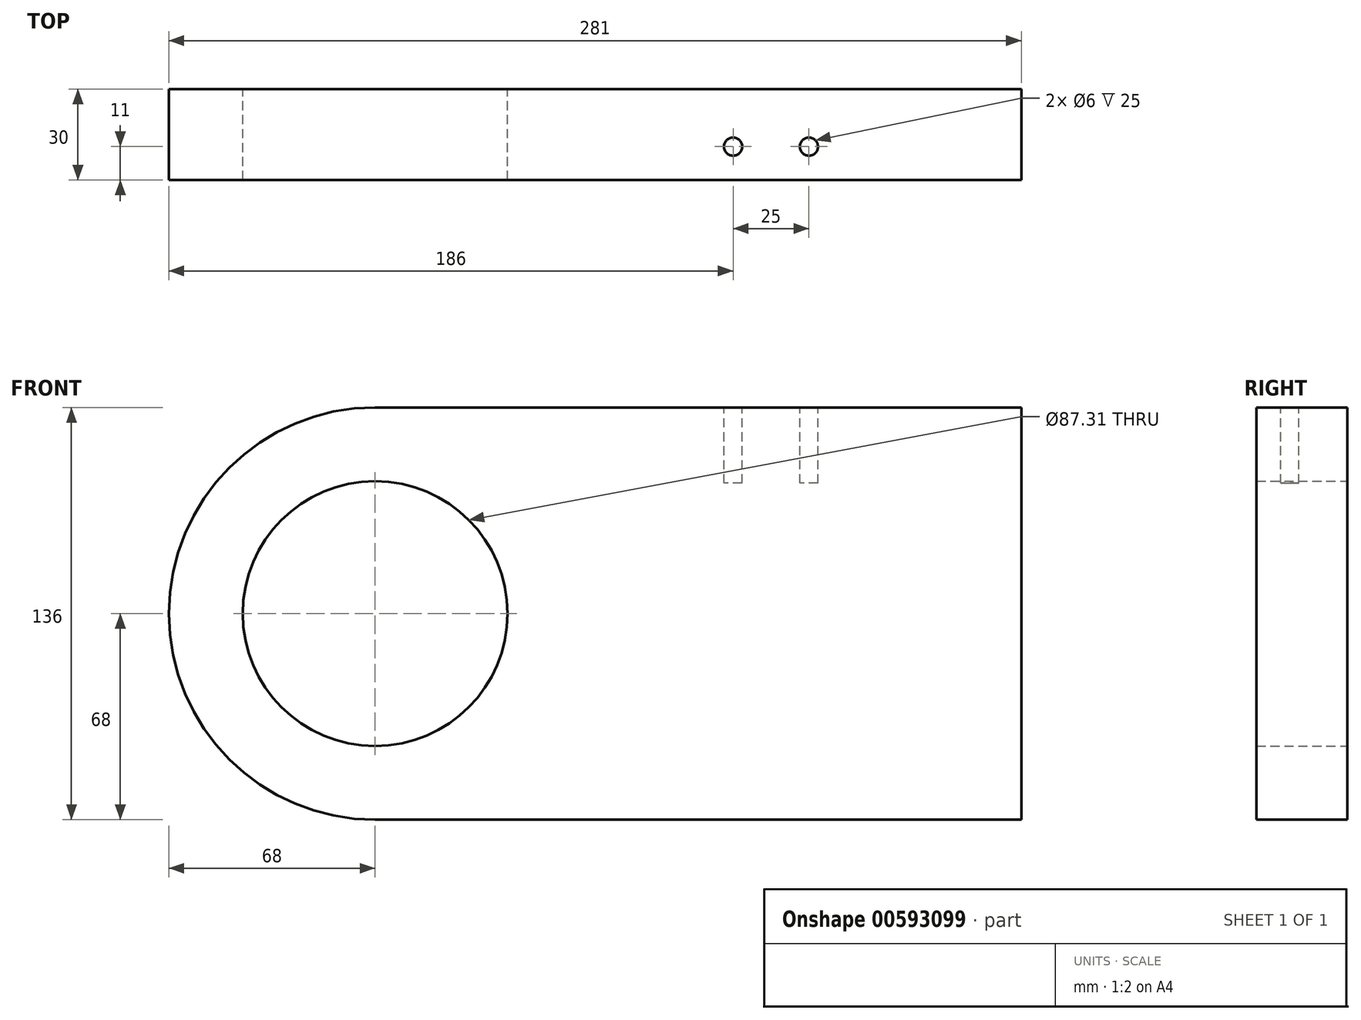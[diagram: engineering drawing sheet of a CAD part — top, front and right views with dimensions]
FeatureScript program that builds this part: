
annotation { "Feature Type Name" : "Feature", "Feature Type Description" : "" }
export const myFeature = defineFeature(function(context is Context, id is Id, definition is map)
    precondition{}
    {
        {
            var Q0;
            Q0=qCreatedBy(makeId("Front.planeOp"),FACE);
            var sketch = newSketch(context, id + "F0", { "sketchPlane" : qUnion([Q0])});
            skLineSegment(sketch, "E0.bottom", {"start": v(106.5, 68) * mm, "end": v(-106.5, 68) * mm});
            skLineSegment(sketch, "E0.top", {"start": v(106.5, -68) * mm, "end": v(-106.5, -68) * mm});
            skLineSegment(sketch, "E0.left", {"start": v(106.5, 68) * mm, "end": v(106.5, -68) * mm});
            skArc(sketch, "E1", {"start": v(-106.5, 68) * mm, "mid": v(-174.5, 0) * mm, "end": v(-106.5, -68) * mm});
            skCircle(sketch, "E2", {"center": v(-106.5, 0) * mm, "radius": 43.66 * mm});
            skSolve(sketch);
        }
        {
            var Q0;
            Q0=makeQuery(id+"F0.imprint","IMPRINT",FACE,{"disambiguationData":[TD([[makeQuery(id+"F0.imprint","IMPRINT",EDGE,{"derivedFrom":sQuery(id+"F0.wireOp",EDGE,"E0.bottom")}),1.0]])]});
            extrude(context, id + "F1", {"entities" : qUnion([Q0]), "depth" : 30 * mm, "offsetDistance" : 25 * mm});
        }
        {
            var Q0;
            Q0=makeQuery(id+"F1.opExtrude","SWEPT_FACE",FACE,{"disambiguationData":[OSD([sQuery(id+"F0.wireOp",EDGE,"E0.bottom")])]});
            var sketch = newSketch(context, id + "F2", { "sketchPlane" : qUnion([Q0])});
            skCircle(sketch, "E3", {"center": v(36.5, -19) * mm, "radius": 3 * mm});
            skCircle(sketch, "E4", {"center": v(11.5, -19) * mm, "radius": 3 * mm});
            skSolve(sketch);
        }
        {
            var Q0;
            Q0=qSketchRegion(id+"F2",true);
            extrude(context, id + "F3", {"entities" : qUnion([Q0]), "operationType" : NewBodyOperationType.REMOVE, "oppositeDirection" : true, "depth" : 25 * mm, "offsetDistance" : 25 * mm});
        }
    });
